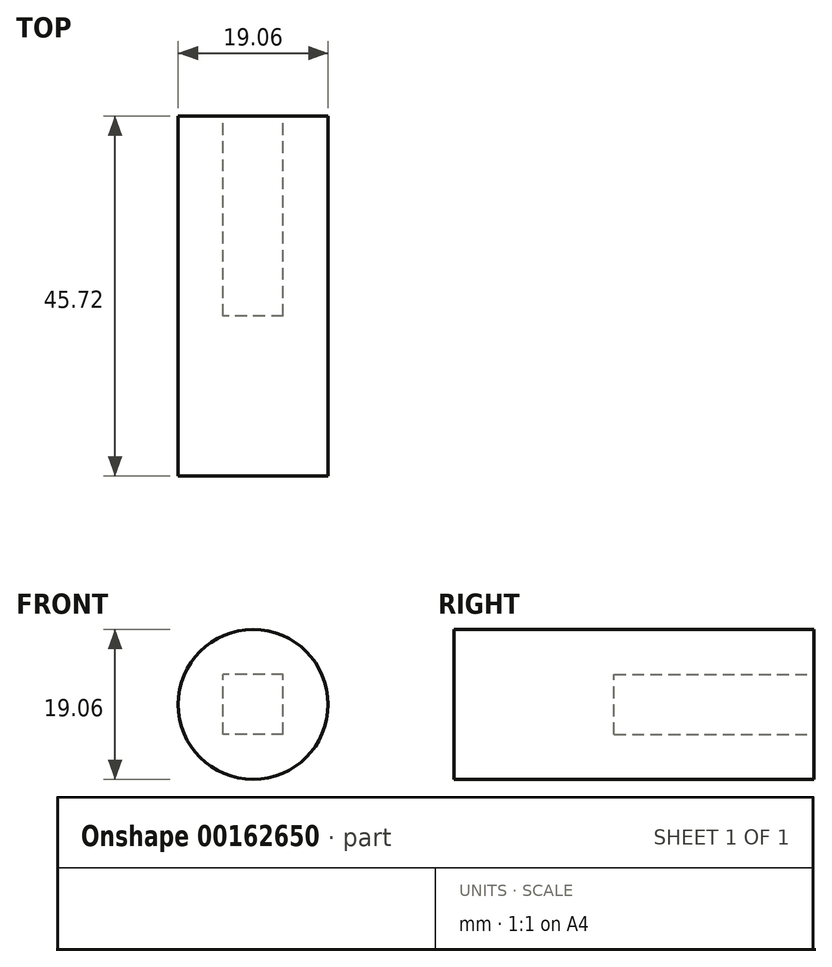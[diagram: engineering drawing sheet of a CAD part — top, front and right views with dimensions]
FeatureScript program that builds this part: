
annotation { "Feature Type Name" : "Feature", "Feature Type Description" : "" }
export const myFeature = defineFeature(function(context is Context, id is Id, definition is map)
    precondition{}
    {
        {
            var Q0;
            Q0=qCreatedBy(makeId("Front.planeOp"),FACE);
            var sketch = newSketch(context, id + "F0", { "sketchPlane" : qUnion([Q0])});
            skCircle(sketch, "E0", {"center": v(0, 0) * mm, "radius": 9.52 * mm});
            skSolve(sketch);
        }
        {
            var Q0;
            Q0 = qSketchRegion(id + "F0", true);
            extrude(context, id + "F1", {"entities" : qUnion([Q0]), "depth" : 45.72 * mm});
        }
        {
            var Q0;
            Q0=qCreatedBy(makeId("Front.planeOp"),FACE);
            var sketch = newSketch(context, id + "F2", { "sketchPlane" : qUnion([Q0])});
            skLineSegment(sketch, "E1.bottom", {"start": v(3.8, -3.81) * mm, "end": v(-3.81, -3.81) * mm});
            skLineSegment(sketch, "E1.top", {"start": v(3.81, 3.81) * mm, "end": v(-3.8, 3.81) * mm});
            skLineSegment(sketch, "E1.left", {"start": v(3.81, -3.8) * mm, "end": v(3.81, 3.81) * mm});
            skLineSegment(sketch, "E1.right", {"start": v(-3.81, -3.81) * mm, "end": v(-3.81, 3.8) * mm});
            skPoint(sketch, "E1.middle", {"position": v(0, 0) * mm});
            skCircle(sketch, "E2", {"center": v(0, 0) * mm, "radius": 3.8 * mm});
            skSolve(sketch);
        }
        {
            var Q0;
            {var subQ0=sQuery(id+"F2.wireOp",EDGE,"E1.left");var subQ1=sQuery(id+"F2.wireOp",EDGE,"E1.top");var subQ2=makeQuery(id+"F2.imprint","INTERSECT",VERTEX,{"derivedFrom":[subQ1,subQ0]});Q0=makeQuery(id+"F2.imprint","IMPRINT",FACE,{"disambiguationData":[TD([[makeQuery(id+"F2.imprint","IMPRINT",EDGE,{"disambiguationData":[TD([[subQ2,-1.0]])],"derivedFrom":subQ1}),1.0]])]});}
            var Q1;
            {var subQ0=sQuery(id+"F2.wireOp",EDGE,"E1.left");var subQ1=sQuery(id+"F2.wireOp",EDGE,"E1.bottom");var subQ2=makeQuery(id+"F2.imprint","INTERSECT",VERTEX,{"derivedFrom":[subQ1,subQ0]});Q1=makeQuery(id+"F2.imprint","IMPRINT",FACE,{"disambiguationData":[TD([[makeQuery(id+"F2.imprint","IMPRINT",EDGE,{"disambiguationData":[TD([[subQ2,-1.0]])],"derivedFrom":subQ1}),-1.0]])]});}
            var Q2;
            {var subQ0=sQuery(id+"F2.wireOp",EDGE,"E1.right");var subQ1=sQuery(id+"F2.wireOp",EDGE,"E1.bottom");var subQ2=makeQuery(id+"F2.imprint","INTERSECT",VERTEX,{"derivedFrom":[subQ1,subQ0]});Q2=makeQuery(id+"F2.imprint","IMPRINT",FACE,{"disambiguationData":[TD([[makeQuery(id+"F2.imprint","IMPRINT",EDGE,{"disambiguationData":[TD([[subQ2,1.0]])],"derivedFrom":subQ1}),-1.0]])]});}
            var Q3;
            {var subQ0=sQuery(id+"F2.wireOp",EDGE,"E2");var subQ1=makeQuery(id+"F2.imprint","INTERSECT",VERTEX,{"derivedFrom":[sQuery(id+"F2.wireOp",EDGE,"E1.top"),subQ0]});Q3=makeQuery(id+"F2.imprint","IMPRINT",FACE,{"disambiguationData":[TD([[makeQuery(id+"F2.imprint","IMPRINT",EDGE,{"disambiguationData":[TD([[subQ1,1.0]])],"derivedFrom":subQ0}),1.0]])]});}
            var Q4;
            {var subQ0=sQuery(id+"F2.wireOp",EDGE,"E1.right");var subQ1=sQuery(id+"F2.wireOp",EDGE,"E1.top");var subQ2=makeQuery(id+"F2.imprint","INTERSECT",VERTEX,{"derivedFrom":[subQ1,subQ0]});Q4=makeQuery(id+"F2.imprint","IMPRINT",FACE,{"disambiguationData":[TD([[makeQuery(id+"F2.imprint","IMPRINT",EDGE,{"disambiguationData":[TD([[subQ2,1.0]])],"derivedFrom":subQ1}),1.0]])]});}
            var Q5;
            Q5=sQuery(id+"F2.wireOp",EDGE,"E1.top");
            var Q6;
            Q6=sQuery(id+"F2.wireOp",EDGE,"E1.left");
            var Q7;
            Q7=sQuery(id+"F2.wireOp",EDGE,"E1.bottom");
            var Q8;
            Q8=sQuery(id+"F2.wireOp",EDGE,"E1.right");
            extrude(context, id + "F3", {"entities" : qUnion([Q0, Q1, Q2, Q3, Q4]), "operationType" : NewBodyOperationType.REMOVE, "surfaceEntities" : qUnion([Q5, Q6, Q7, Q8]), "depth" : 25.4 * mm});
        }
    });
